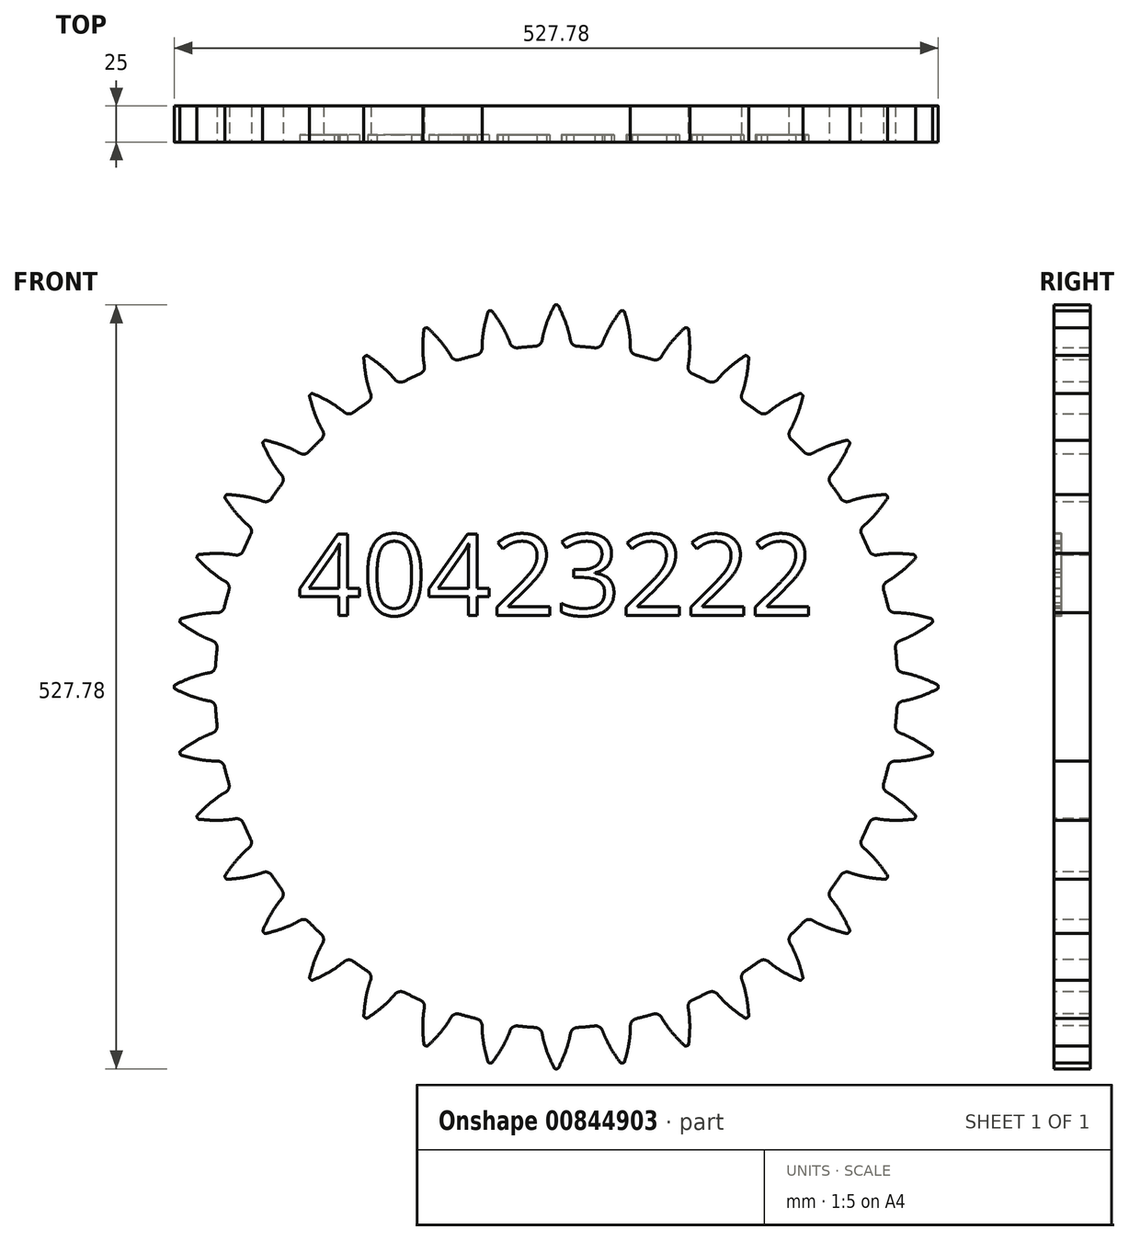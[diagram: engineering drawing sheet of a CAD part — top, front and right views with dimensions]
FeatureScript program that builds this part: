
annotation { "Feature Type Name" : "Feature", "Feature Type Description" : "" }
export const myFeature = defineFeature(function(context is Context, id is Id, definition is map)
    precondition{}
    {
        {
            var Q0;
            Q0=qCreatedBy(makeId("Front.planeOp"),FACE);
            var sketch = newSketch(context, id + "F0", { "sketchPlane" : qUnion([Q0])});
            skLineSegment(sketch, "E0.bottom", {"start": v(400, 300) * mm, "end": v(-400, 300) * mm});
            skLineSegment(sketch, "E0.top", {"start": v(400, -300) * mm, "end": v(-400, -300) * mm});
            skLineSegment(sketch, "E0.left", {"start": v(400, 300) * mm, "end": v(400, -300) * mm});
            skLineSegment(sketch, "E0.right", {"start": v(-400, 300) * mm, "end": v(-400, -300) * mm});
            skPoint(sketch, "E0.middle", {"position": v(0, 0) * mm});
            skCircle(sketch, "E1", {"center": v(0, 0) * mm, "radius": 250 * mm});
            skText(sketch, "E2", { "text": "Module = 500/36 = 13.888", "fontName": "OpenSans-Regular.ttf"});
            skCircle(sketch, "E3.0", {"center": v(0, 0) * mm, "radius": 263.89 * mm});
            skCircle(sketch, "E4.0", {"center": v(0, 0) * mm, "radius": 235.81 * mm});
            skPoint(sketch, "E5", {"position": v(29.73, 248.23) * mm});
            skArc(sketch, "E6", {"start": v(-38.46, 231.75) * mm, "mid": v(0.39, -234.92) * mm, "end": v(37.69, 231.88) * mm});
            skLineSegment(sketch, "E7", {"start": v(106.03, 209.63) * mm, "end": v(0, 0) * mm});
            skLineSegment(sketch, "E8", {"start": v(84.05, 219.37) * mm, "end": v(0, 0) * mm});
            skLineSegment(sketch, "E9", {"start": v(61.2, 226.81) * mm, "end": v(0, 0) * mm});
            skLineSegment(sketch, "E10", {"start": v(37.69, 231.88) * mm, "end": v(0, 0) * mm});
            skFitSpline(sketch, "E11", {"points": [v(-10.25, 234.7) * mm, v(-10.2, 235.93) * mm, v(-9.77, 239.6) * mm, v(-8.44, 245.6) * mm, v(-5.74, 253.78) * mm, v(-1.23, 263.89) * mm], "startDerivative": vector(-1.24, 11.37) * mm, "endDerivative": vector(17.19, 36.05) * mm});
            skLineSegment(sketch, "E12", {"start": v(0, -334.79) * mm, "end": v(0, 396.98) * mm, "construction": true});
            skFitSpline(sketch, "E13.MirrorCS", {"points": [v(10.25, 234.7) * mm, v(10.2, 235.93) * mm, v(9.77, 239.6) * mm, v(8.44, 245.6) * mm, v(5.74, 253.78) * mm, v(1.23, 263.89) * mm], "startDerivative": vector(1.24, 11.37) * mm, "endDerivative": vector(-17.19, 36.05) * mm});
            skLineSegment(sketch, "E14", {"start": v(-10.24, 235.59) * mm, "end": v(0, 0) * mm});
            skLineSegment(sketch, "E15", {"start": v(10.24, 235.59) * mm, "end": v(0, 0) * mm});
            skLineSegment(sketch, "E16", {"start": v(0, 0) * mm, "end": v(-38.6, 232.63) * mm});
            skLineSegment(sketch, "E17", {"start": v(37.69, 231.88) * mm, "end": v(37.83, 232.76) * mm});
            const initialGuessF0  = {"E2": [-0.85754, 0.4595, 1, 0, 0.10541]};
            skSetInitialGuess(sketch, initialGuessF0);
            skSolve(sketch);
        }
        {
            var Q0;
            {var subQ0=sQuery(id+"F0.wireOp",EDGE,"E11");var subQ1=sQuery(id+"F0.wireOp",EDGE,"E1");var subQ2=makeQuery(id+"F0.imprint","INTERSECT",VERTEX,{"derivedFrom":[subQ1,subQ0]});Q0=makeQuery(id+"F0.imprint","IMPRINT",FACE,{"disambiguationData":[TD([[makeQuery(id+"F0.imprint","IMPRINT",EDGE,{"disambiguationData":[TD([[subQ2,1.0]])],"derivedFrom":subQ1}),1.0]])]});}
            var Q1;
            {var subQ0=sQuery(id+"F0.wireOp",EDGE,"E11");var subQ1=sQuery(id+"F0.wireOp",EDGE,"E1");var subQ2=makeQuery(id+"F0.imprint","INTERSECT",VERTEX,{"derivedFrom":[subQ1,subQ0]});Q1=makeQuery(id+"F0.imprint","IMPRINT",FACE,{"disambiguationData":[TD([[makeQuery(id+"F0.imprint","IMPRINT",EDGE,{"disambiguationData":[TD([[subQ2,1.0]])],"derivedFrom":subQ1}),-1.0]])]});}
            var Q2;
            {var subQ0=sQuery(id+"F0.wireOp",EDGE,"E14");Q2=makeQuery(id+"F0.imprint","IMPRINT",FACE,{"disambiguationData":[TD([[makeQuery(id+"F0.imprint","IMPRINT",EDGE,{"derivedFrom":subQ0}),1.0]])]});}
            var Q3;
            {var subQ0=sQuery(id+"F0.wireOp",EDGE,"E14");Q3=makeQuery(id+"F0.imprint","IMPRINT",FACE,{"disambiguationData":[TD([[makeQuery(id+"F0.imprint","IMPRINT",EDGE,{"derivedFrom":subQ0}),-1.0]])]});}
            var Q4;
            Q4=makeQuery(id+"F0.imprint","IMPRINT",FACE,{"disambiguationData":[TD([[makeQuery(id+"F0.imprint","IMPRINT",EDGE,{"derivedFrom":sQuery(id+"F0.wireOp",EDGE,"E10")}),-1.0]])]});
            extrude(context, id + "F1", {"entities" : qUnion([Q0, Q1, Q2, Q3, Q4]), "oppositeDirection" : true, "depth" : 25 * mm, "offsetDistance" : 25 * mm});
        }
        {
            var Q0;
            Q0=makeQuery(id+"F1.opExtrude","SWEPT_EDGE",EDGE,{"disambiguationData":[OSD([sQuery(id+"F0.wireOp",EDGE,"E3.0"),sQuery(id+"F0.wireOp",EDGE,"E13.MirrorCS")])]});
            var Q1;
            Q1=makeQuery(id+"F1.opExtrude","SWEPT_EDGE",EDGE,{"disambiguationData":[OSD([sQuery(id+"F0.wireOp",EDGE,"E3.0"),sQuery(id+"F0.wireOp",EDGE,"E11")])]});
            fillet(context, id + "F2", {"entities" : qUnion([Q0, Q1]), "radius" : 1 * mm, "tangentPropagation" : true, "allowEdgeOverflow" : false});
        }
        {
            var Q0;
            Q0=makeQuery(id+"F1.opExtrude","SWEPT_EDGE",EDGE,{"disambiguationData":[OSD([sQuery(id+"F0.wireOp",EDGE,"E4.0"),sQuery(id+"F0.wireOp",EDGE,"E13.MirrorCS"),sQuery(id+"F0.wireOp",EDGE,"E15")])]});
            var Q1;
            Q1=makeQuery(id+"F1.opExtrude","SWEPT_EDGE",EDGE,{"disambiguationData":[OSD([sQuery(id+"F0.wireOp",EDGE,"E4.0"),sQuery(id+"F0.wireOp",EDGE,"E11"),sQuery(id+"F0.wireOp",EDGE,"E14")])]});
            fillet(context, id + "F3", {"entities" : qUnion([Q0, Q1]), "radius" : 5 * mm, "tangentPropagation" : true, "allowEdgeOverflow" : false});
        }
        {
            var Q0;
            Q0=qCreatedBy(makeId("Top.planeOp"),FACE);
            var sketch = newSketch(context, id + "F4", { "sketchPlane" : qUnion([Q0])});
            skLineSegment(sketch, "E18", {"start": v(0, 43.7) * mm, "end": v(0, -32.4) * mm, "construction": true});
            skSolve(sketch);
        }
        {
            var Q0;
            Q0=makeQuery(id+"F1.opExtrude","SWEPT_BODY",BODY,{"disambiguationData":[OSD([sQuery(id+"F0.wireOp",EDGE,"E3.0"),sQuery(id+"F0.wireOp",EDGE,"E4.0"),sQuery(id+"F0.wireOp",EDGE,"E10"),sQuery(id+"F0.wireOp",EDGE,"E11"),sQuery(id+"F0.wireOp",EDGE,"E13.MirrorCS"),sQuery(id+"F0.wireOp",EDGE,"E16"),sQuery(id+"F0.wireOp",EDGE,"E17")])]});
            var Q1;
            Q1=sQuery(id+"F4.wireOp",EDGE,"E18");
            circularPattern(context, id + "F5", {"operationType" : NewBodyOperationType.ADD, "entities" : qUnion([Q0]), "axis" : qUnion([Q1]), "angle" : 360 * degree, "instanceCount" : 36, "equalSpace" : true});
        }
        {
            var Q0;
            {var subQ0=makeQuery(id+"F1.opExtrude","CAP_FACE",FACE,{"disambiguationData":[OSD([sQuery(id+"F0.wireOp",EDGE,"E3.0"),sQuery(id+"F0.wireOp",EDGE,"E4.0"),sQuery(id+"F0.wireOp",EDGE,"E10"),sQuery(id+"F0.wireOp",EDGE,"E11"),sQuery(id+"F0.wireOp",EDGE,"E13.MirrorCS"),sQuery(id+"F0.wireOp",EDGE,"E16"),sQuery(id+"F0.wireOp",EDGE,"E17")])],"isStart":true});Q0=makeQuery(id+"F5.boolean.opBoolean","MERGE",FACE,{"derivedFrom":[subQ0,makeQuery(id+"F5.opPattern","COPY",FACE,{"derivedFrom":subQ0,"instanceName":"1"}),makeQuery(id+"F5.opPattern","COPY",FACE,{"derivedFrom":subQ0,"instanceName":"2"}),makeQuery(id+"F5.opPattern","COPY",FACE,{"derivedFrom":subQ0,"instanceName":"3"}),makeQuery(id+"F5.opPattern","COPY",FACE,{"derivedFrom":subQ0,"instanceName":"4"}),makeQuery(id+"F5.opPattern","COPY",FACE,{"derivedFrom":subQ0,"instanceName":"5"}),makeQuery(id+"F5.opPattern","COPY",FACE,{"derivedFrom":subQ0,"instanceName":"6"}),makeQuery(id+"F5.opPattern","COPY",FACE,{"derivedFrom":subQ0,"instanceName":"7"}),makeQuery(id+"F5.opPattern","COPY",FACE,{"derivedFrom":subQ0,"instanceName":"8"}),makeQuery(id+"F5.opPattern","COPY",FACE,{"derivedFrom":subQ0,"instanceName":"9"}),makeQuery(id+"F5.opPattern","COPY",FACE,{"derivedFrom":subQ0,"instanceName":"10"}),makeQuery(id+"F5.opPattern","COPY",FACE,{"derivedFrom":subQ0,"instanceName":"11"}),makeQuery(id+"F5.opPattern","COPY",FACE,{"derivedFrom":subQ0,"instanceName":"12"}),makeQuery(id+"F5.opPattern","COPY",FACE,{"derivedFrom":subQ0,"instanceName":"13"}),makeQuery(id+"F5.opPattern","COPY",FACE,{"derivedFrom":subQ0,"instanceName":"14"}),makeQuery(id+"F5.opPattern","COPY",FACE,{"derivedFrom":subQ0,"instanceName":"15"}),makeQuery(id+"F5.opPattern","COPY",FACE,{"derivedFrom":subQ0,"instanceName":"16"}),makeQuery(id+"F5.opPattern","COPY",FACE,{"derivedFrom":subQ0,"instanceName":"17"}),makeQuery(id+"F5.opPattern","COPY",FACE,{"derivedFrom":subQ0,"instanceName":"18"}),makeQuery(id+"F5.opPattern","COPY",FACE,{"derivedFrom":subQ0,"instanceName":"19"}),makeQuery(id+"F5.opPattern","COPY",FACE,{"derivedFrom":subQ0,"instanceName":"20"}),makeQuery(id+"F5.opPattern","COPY",FACE,{"derivedFrom":subQ0,"instanceName":"21"}),makeQuery(id+"F5.opPattern","COPY",FACE,{"derivedFrom":subQ0,"instanceName":"22"}),makeQuery(id+"F5.opPattern","COPY",FACE,{"derivedFrom":subQ0,"instanceName":"23"}),makeQuery(id+"F5.opPattern","COPY",FACE,{"derivedFrom":subQ0,"instanceName":"24"}),makeQuery(id+"F5.opPattern","COPY",FACE,{"derivedFrom":subQ0,"instanceName":"25"}),makeQuery(id+"F5.opPattern","COPY",FACE,{"derivedFrom":subQ0,"instanceName":"26"}),makeQuery(id+"F5.opPattern","COPY",FACE,{"derivedFrom":subQ0,"instanceName":"27"}),makeQuery(id+"F5.opPattern","COPY",FACE,{"derivedFrom":subQ0,"instanceName":"28"}),makeQuery(id+"F5.opPattern","COPY",FACE,{"derivedFrom":subQ0,"instanceName":"29"}),makeQuery(id+"F5.opPattern","COPY",FACE,{"derivedFrom":subQ0,"instanceName":"30"}),makeQuery(id+"F5.opPattern","COPY",FACE,{"derivedFrom":subQ0,"instanceName":"31"}),makeQuery(id+"F5.opPattern","COPY",FACE,{"derivedFrom":subQ0,"instanceName":"32"}),makeQuery(id+"F5.opPattern","COPY",FACE,{"derivedFrom":subQ0,"instanceName":"33"}),makeQuery(id+"F5.opPattern","COPY",FACE,{"derivedFrom":subQ0,"instanceName":"34"}),makeQuery(id+"F5.opPattern","COPY",FACE,{"derivedFrom":subQ0,"instanceName":"35"})]});}
            var sketch = newSketch(context, id + "F6", { "sketchPlane" : qUnion([Q0])});
            skText(sketch, "E19", { "text": "40423222", "fontName": "OpenSans-Regular.ttf"});
            const initialGuessF6  = {"E19": [-0.17885, 0.0495, 1, 0, 0.05624]};
            skSetInitialGuess(sketch, initialGuessF6);
            skSolve(sketch);
        }
        {
            var Q0;
            Q0 = qSketchRegion(id + "F6", true);
            extrude(context, id + "F7", {"entities" : qUnion([Q0]), "operationType" : NewBodyOperationType.REMOVE, "oppositeDirection" : true, "depth" : 5 * mm, "offsetDistance" : 25 * mm});
        }
    });
